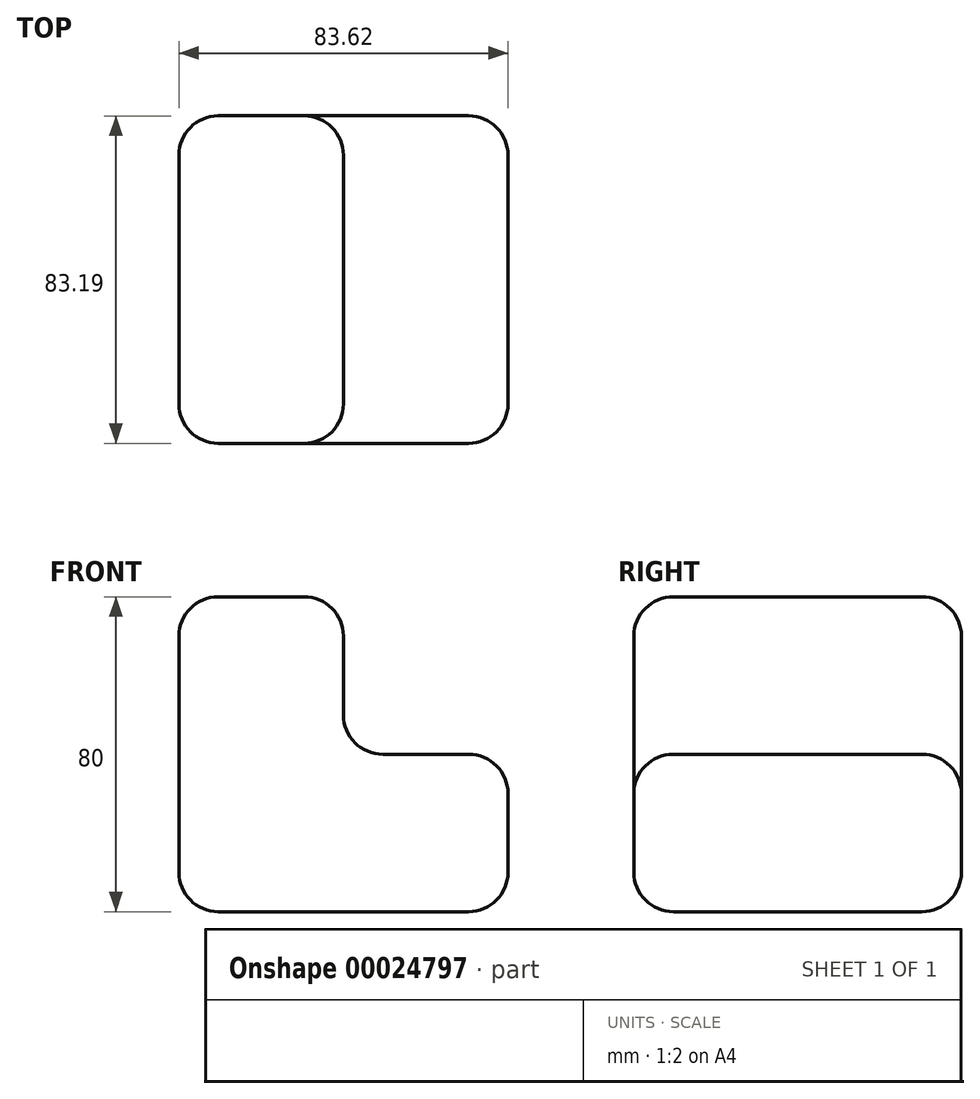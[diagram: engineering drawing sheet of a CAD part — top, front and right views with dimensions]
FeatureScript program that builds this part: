
annotation { "Feature Type Name" : "Feature", "Feature Type Description" : "" }
export const myFeature = defineFeature(function(context is Context, id is Id, definition is map)
    precondition{}
    {
        {
            var Q0;
            Q0=qCreatedBy(makeId("Top.planeOp"),FACE);
            var sketch = newSketch(context, id + "F0", { "sketchPlane" : qUnion([Q0])});
            skLineSegment(sketch, "E0.bottom", {"start": v(-59.13, -45.93) * mm, "end": v(24.5, -45.93) * mm});
            skLineSegment(sketch, "E0.top", {"start": v(-59.13, 37.26) * mm, "end": v(24.5, 37.26) * mm});
            skLineSegment(sketch, "E0.left", {"start": v(-59.13, -45.93) * mm, "end": v(-59.13, 37.26) * mm});
            skLineSegment(sketch, "E0.right", {"start": v(24.5, -45.93) * mm, "end": v(24.5, 37.26) * mm});
            skSolve(sketch);
        }
        {
            var Q0;
            Q0=makeQuery(id+"F0.imprint","IMPRINT",FACE,{"disambiguationData":[TD([[makeQuery(id+"F0.imprint","IMPRINT",EDGE,{"derivedFrom":sQuery(id+"F0.wireOp",EDGE,"E0.bottom")}),1.0]])]});
            extrude(context, id + "F1", {"entities" : qUnion([Q0]), "depth" : 40 * mm});
        }
        {
            var Q0;
            Q0=makeQuery(id+"F1.opExtrude","CAP_FACE",FACE,{"disambiguationData":[OSD([sQuery(id+"F0.wireOp",EDGE,"E0.bottom"),sQuery(id+"F0.wireOp",EDGE,"E0.top"),sQuery(id+"F0.wireOp",EDGE,"E0.left"),sQuery(id+"F0.wireOp",EDGE,"E0.right")])],"isStart":false});
            var sketch = newSketch(context, id + "F2", { "sketchPlane" : qUnion([Q0])});
            skLineSegment(sketch, "E1", {"start": v(-17.32, 37.26) * mm, "end": v(-17.32, -45.93) * mm});
            skSolve(sketch);
        }
        {
            var Q0;
            {var subQ1=sQuery(id+"F2.wireOp",EDGE,"E1");Q0=makeQuery(id+"F2.imprint","IMPRINT",FACE,{"disambiguationData":[TD([[makeQuery(id+"F2.imprint","IMPRINT",EDGE,{"derivedFrom":subQ1}),-1.0]])]});}
            extrude(context, id + "F3", {"entities" : qUnion([Q0]), "operationType" : NewBodyOperationType.ADD, "depth" : 40 * mm});
        }
        {
            var Q0;
            Q0=makeQuery(id+"F3.opExtrude","CAP_FACE",FACE,{"disambiguationData":[OSD([sQuery(id+"F0.wireOp",EDGE,"E0.bottom"),sQuery(id+"F0.wireOp",EDGE,"E0.top"),sQuery(id+"F0.wireOp",EDGE,"E0.left"),sQuery(id+"F2.wireOp",EDGE,"E1")])],"isStart":false});
            var Q1;
            {var subQ0=sQuery(id+"F0.wireOp",EDGE,"E0.bottom");Q1=makeQuery(id+"F3.boolean.opBoolean","MERGE",FACE,{"derivedFrom":[makeQuery(id+"F1.opExtrude","SWEPT_FACE",FACE,{"disambiguationData":[OSD([subQ0])]}),makeQuery(id+"F3.opExtrude","SWEPT_FACE",FACE,{"disambiguationData":[OSD([subQ0])]})]});}
            var Q2;
            Q2=makeQuery(id+"F1.opExtrude","CAP_FACE",FACE,{"disambiguationData":[OSD([sQuery(id+"F0.wireOp",EDGE,"E0.bottom"),sQuery(id+"F0.wireOp",EDGE,"E0.top"),sQuery(id+"F0.wireOp",EDGE,"E0.left"),sQuery(id+"F0.wireOp",EDGE,"E0.right")])],"isStart":false});
            var Q3;
            Q3=makeQuery(id+"F1.opExtrude","SWEPT_FACE",FACE,{"disambiguationData":[OSD([sQuery(id+"F0.wireOp",EDGE,"E0.right")])]});
            var Q4;
            {var subQ0=sQuery(id+"F0.wireOp",EDGE,"E0.left");Q4=makeQuery(id+"F3.boolean.opBoolean","MERGE",FACE,{"derivedFrom":[makeQuery(id+"F1.opExtrude","SWEPT_FACE",FACE,{"disambiguationData":[OSD([subQ0])]}),makeQuery(id+"F3.opExtrude","SWEPT_FACE",FACE,{"disambiguationData":[OSD([subQ0])]})]});}
            var Q5;
            Q5=makeQuery(id+"F1.opExtrude","CAP_FACE",FACE,{"disambiguationData":[OSD([sQuery(id+"F0.wireOp",EDGE,"E0.bottom"),sQuery(id+"F0.wireOp",EDGE,"E0.top"),sQuery(id+"F0.wireOp",EDGE,"E0.left"),sQuery(id+"F0.wireOp",EDGE,"E0.right")])],"isStart":true});
            var Q6;
            {var subQ0=sQuery(id+"F0.wireOp",EDGE,"E0.top");Q6=makeQuery(id+"F3.boolean.opBoolean","MERGE",FACE,{"derivedFrom":[makeQuery(id+"F1.opExtrude","SWEPT_FACE",FACE,{"disambiguationData":[OSD([subQ0])]}),makeQuery(id+"F3.opExtrude","SWEPT_FACE",FACE,{"disambiguationData":[OSD([subQ0])]})]});}
            fillet(context, id + "F4", {"entities" : qUnion([Q0, Q1, Q2, Q3, Q4, Q5, Q6]), "radius" : 10 * mm, "tangentPropagation" : true, "allowEdgeOverflow" : false});
        }
    });
